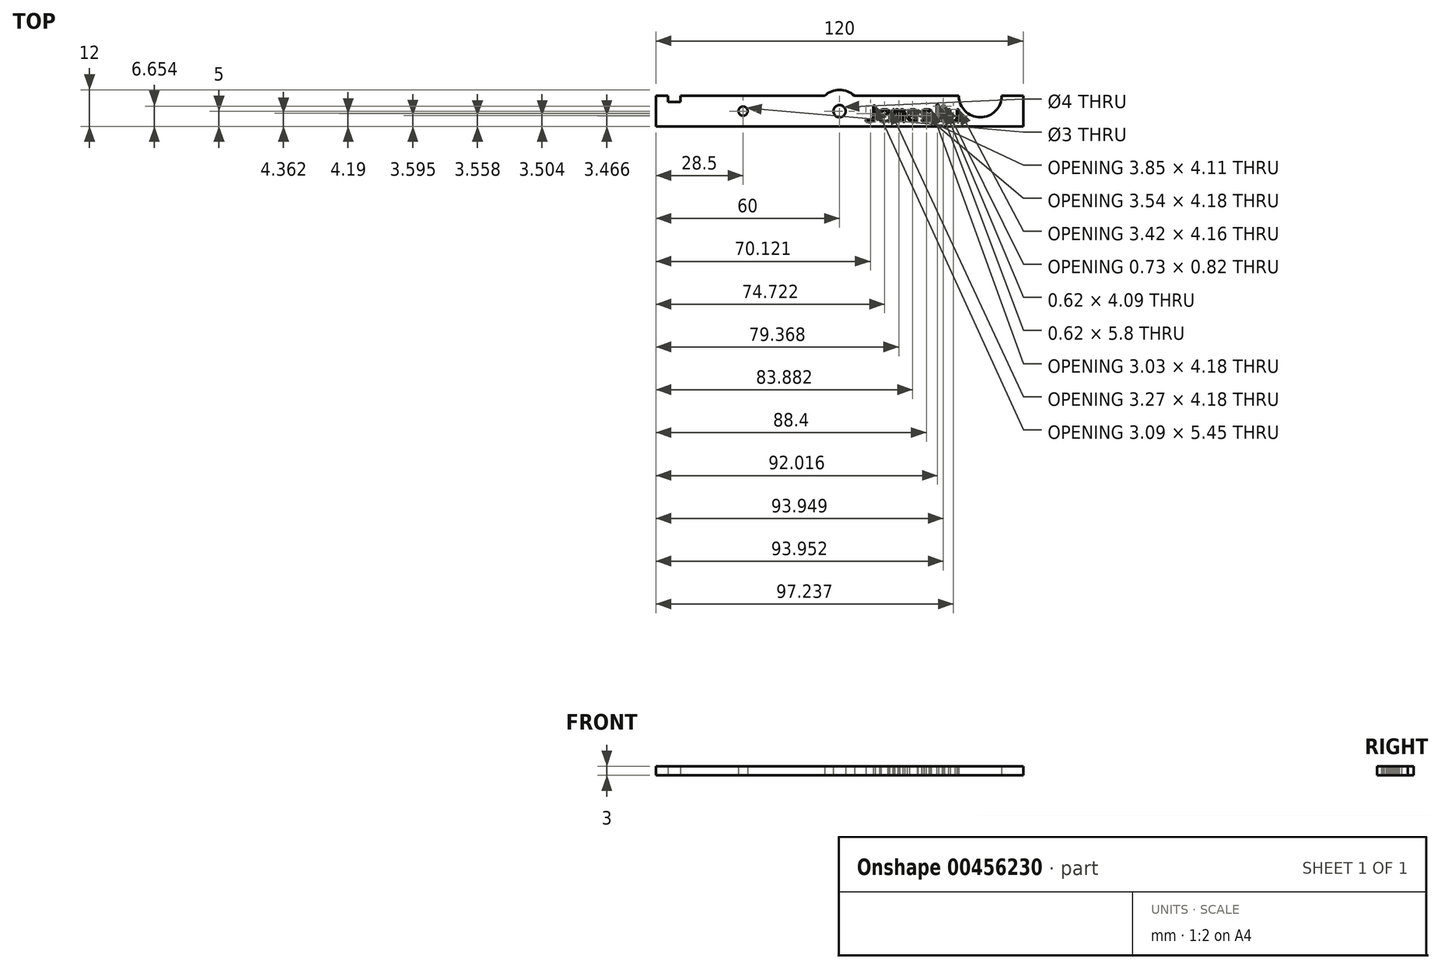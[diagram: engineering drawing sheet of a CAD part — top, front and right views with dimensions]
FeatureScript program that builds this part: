
annotation { "Feature Type Name" : "Feature", "Feature Type Description" : "" }
export const myFeature = defineFeature(function(context is Context, id is Id, definition is map)
    precondition{}
    {
        {
            var Q0;
            Q0=qCreatedBy(makeId("Top.planeOp"),FACE);
            var sketch = newSketch(context, id + "F0", { "sketchPlane" : qUnion([Q0])});
            skLineSegment(sketch, "E0.bottom", {"start": v(-60, 5) * mm, "end": v(60, 5) * mm});
            skLineSegment(sketch, "E0.top", {"start": v(-60, -5) * mm, "end": v(60, -5) * mm});
            skLineSegment(sketch, "E0.left", {"start": v(-60, 5) * mm, "end": v(-60, -5) * mm});
            skLineSegment(sketch, "E0.right", {"start": v(60, 5) * mm, "end": v(60, -5) * mm});
            skPoint(sketch, "E0.middle", {"position": v(0, 0) * mm});
            skLineSegment(sketch, "E1.bottom", {"start": v(-56, 5) * mm, "end": v(-52, 5) * mm});
            skLineSegment(sketch, "E1.top", {"start": v(-56, 3) * mm, "end": v(-52, 3) * mm});
            skLineSegment(sketch, "E1.left", {"start": v(-56, 5) * mm, "end": v(-56, 3) * mm});
            skLineSegment(sketch, "E1.right", {"start": v(-52, 5) * mm, "end": v(-52, 3) * mm});
            skCircle(sketch, "E2", {"center": v(0, 0) * mm, "radius": 2 * mm});
            skCircle(sketch, "E3", {"center": v(0, 0) * mm, "radius": 7 * mm});
            skCircle(sketch, "E4", {"center": v(-31.5, 0) * mm, "radius": 1.5 * mm});
            skCircle(sketch, "E5", {"center": v(46, 5) * mm, "radius": 7 * mm});
            skText(sketch, "E6", { "text": "James", "fontName": "DroidSansMono.ttf"});
            skText(sketch, "E7", { "text": "liu", "fontName": "OpenSans-Regular.ttf"});
            const initialGuessF0  = {"E6": [0.00807, -0.00346, 1, 0, 0.00542], "E7": [0.03105, -0.00354, 1, 0, 0.0055]};
            skSetInitialGuess(sketch, initialGuessF0);
            skSolve(sketch);
        }
        {
            var Q0;
            {var subQ0=sQuery(id+"F0.wireOp",EDGE,"E0.left");Q0=makeQuery(id+"F0.imprint","IMPRINT",FACE,{"disambiguationData":[TD([[makeQuery(id+"F0.imprint","IMPRINT",EDGE,{"derivedFrom":subQ0}),1.0]])]});}
            var Q1;
            Q1=makeQuery(id+"F0.imprint","IMPRINT",FACE,{"disambiguationData":[TD([[makeQuery(id+"F0.imprint","IMPRINT",EDGE,{"derivedFrom":sQuery(id+"F0.wireOp",EDGE,"E2")}),-1.0]])]});
            var Q2;
            {var subQ0=sQuery(id+"F0.wireOp",EDGE,"E3");var subQ1=sQuery(id+"F0.wireOp",EDGE,"E0.bottom");var subQ2=makeQuery(id+"F0.imprint","INTERSECT",VERTEX,{"disambiguationData":[OD(0.0)],"derivedFrom":[subQ1,subQ0]});Q2=makeQuery(id+"F0.imprint","IMPRINT",FACE,{"disambiguationData":[TD([[makeQuery(id+"F0.imprint","IMPRINT",EDGE,{"disambiguationData":[TD([[subQ2,-1.0]])],"derivedFrom":subQ1}),1.0]])]});}
            var Q3;
            {var subQ0=sQuery(id+"F0.wireOp",EDGE,"E3");var subQ1=sQuery(id+"F0.wireOp",EDGE,"E0.top");var subQ2=makeQuery(id+"F0.imprint","INTERSECT",VERTEX,{"disambiguationData":[OD(0.0)],"derivedFrom":[subQ1,subQ0]});Q3=makeQuery(id+"F0.imprint","IMPRINT",FACE,{"disambiguationData":[TD([[makeQuery(id+"F0.imprint","IMPRINT",EDGE,{"disambiguationData":[TD([[subQ2,-1.0]])],"derivedFrom":subQ1}),-1.0]])]});}
            var Q4;
            {var subQ0=sQuery(id+"F0.wireOp",EDGE,"E0.right");Q4=makeQuery(id+"F0.imprint","IMPRINT",FACE,{"disambiguationData":[TD([[makeQuery(id+"F0.imprint","IMPRINT",EDGE,{"derivedFrom":subQ0}),-1.0]])]});}
            extrude(context, id + "F1", {"entities" : qUnion([Q0, Q1, Q2, Q3, Q4]), "depth" : 3 * mm});
        }
    });
